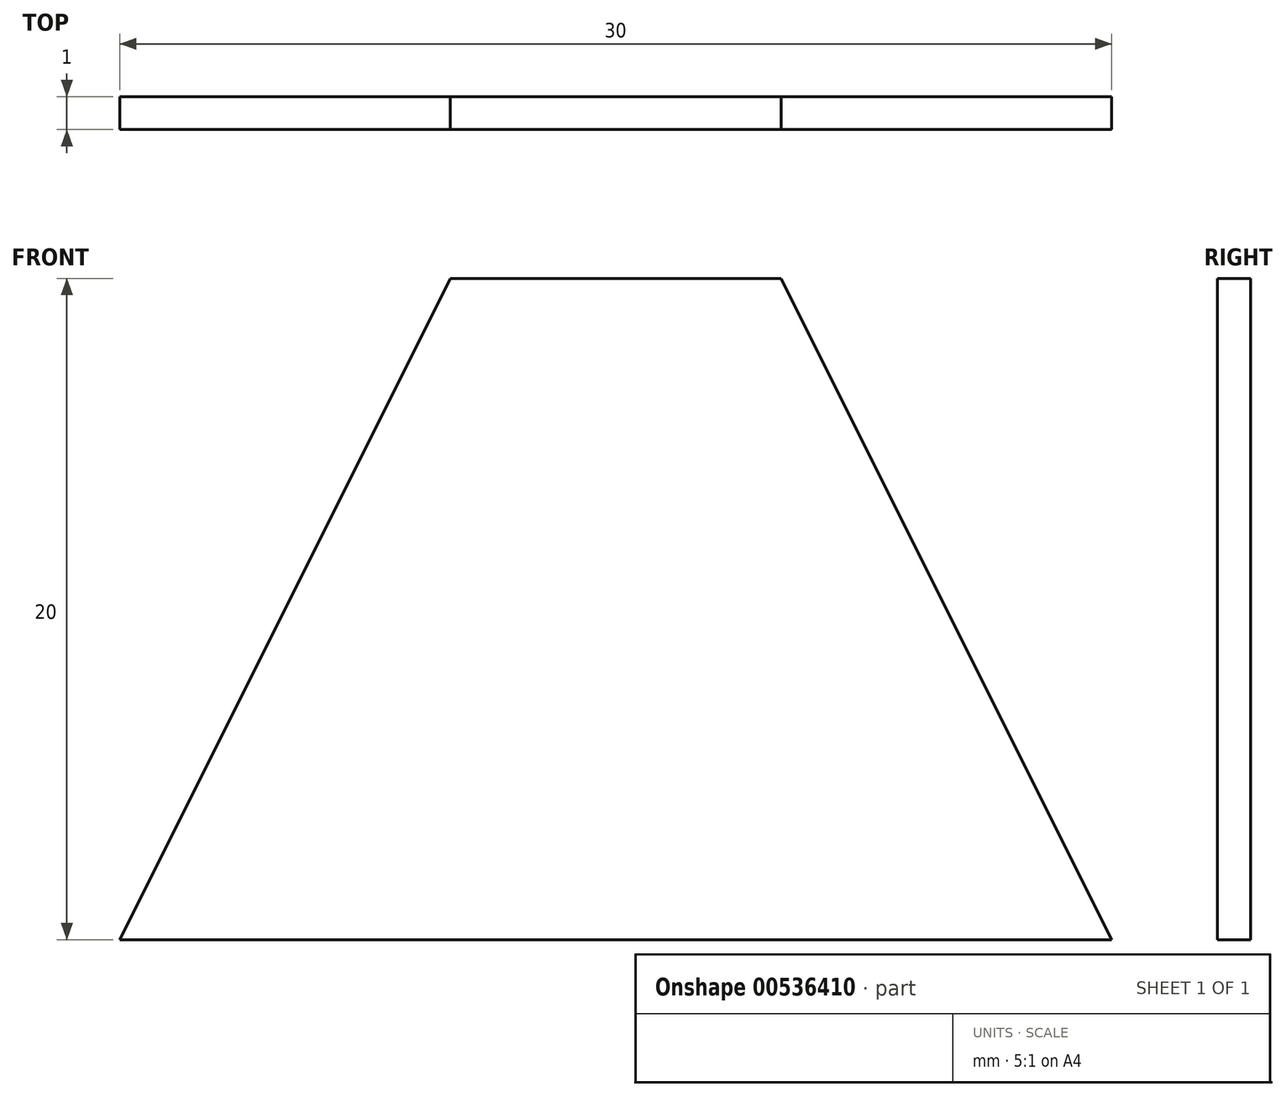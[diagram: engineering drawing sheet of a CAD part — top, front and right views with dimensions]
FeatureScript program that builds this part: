
annotation { "Feature Type Name" : "Feature", "Feature Type Description" : "" }
export const myFeature = defineFeature(function(context is Context, id is Id, definition is map)
    precondition{}
    {
        {
            var Q0;
            Q0=qCreatedBy(makeId("Front.planeOp"),FACE);
            var sketch = newSketch(context, id + "F0", { "sketchPlane" : qUnion([Q0])});
            skLineSegment(sketch, "E0", {"start": v(0, 0) * mm, "end": v(5, 0) * mm});
            skLineSegment(sketch, "E1", {"start": v(0, 0) * mm, "end": v(-5, 0) * mm});
            skLineSegment(sketch, "E2", {"start": v(0, 0) * mm, "end": v(0, -20) * mm});
            skLineSegment(sketch, "E3", {"start": v(0, -20) * mm, "end": v(15, -20) * mm});
            skLineSegment(sketch, "E4", {"start": v(0, -20) * mm, "end": v(-15, -20) * mm});
            skLineSegment(sketch, "E5", {"start": v(-5, 0) * mm, "end": v(-15, -20) * mm});
            skLineSegment(sketch, "E6", {"start": v(5, 0) * mm, "end": v(15, -20) * mm});
            skSolve(sketch);
        }
        {
            var Q0;
            Q0=qSketchRegion(id+"F0",true);
            extrude(context, id + "F1", {"entities" : qUnion([Q0]), "depth" : 1 * mm});
        }
    });
